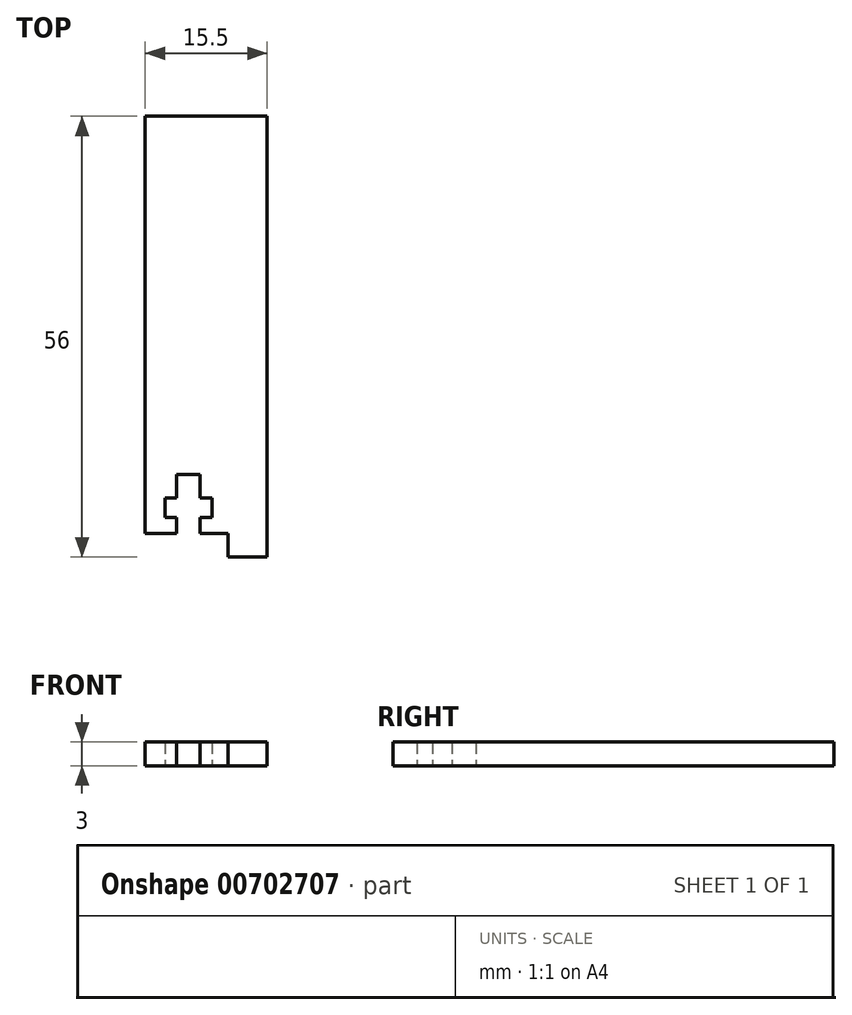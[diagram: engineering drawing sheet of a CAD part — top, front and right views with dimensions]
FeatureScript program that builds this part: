
annotation { "Feature Type Name" : "Feature", "Feature Type Description" : "" }
export const myFeature = defineFeature(function(context is Context, id is Id, definition is map)
    precondition{}
    {
        {
            var Q0;
            Q0=qCreatedBy(makeId("Top.planeOp"),FACE);
            var sketch = newSketch(context, id + "F0", { "sketchPlane" : qUnion([Q0])});
            skLineSegment(sketch, "E0", {"start": v(0, 0) * mm, "end": v(0, 53) * mm});
            skLineSegment(sketch, "E1", {"start": v(0, 53) * mm, "end": v(15.5, 53) * mm});
            skLineSegment(sketch, "E2", {"start": v(15.5, 53) * mm, "end": v(15.5, -3) * mm});
            skLineSegment(sketch, "E3", {"start": v(7, 0) * mm, "end": v(7, 2) * mm});
            skLineSegment(sketch, "E4", {"start": v(7, 2) * mm, "end": v(8.5, 2) * mm});
            skLineSegment(sketch, "E5", {"start": v(8.5, 2) * mm, "end": v(8.5, 4.5) * mm});
            skLineSegment(sketch, "E6", {"start": v(8.5, 4.5) * mm, "end": v(7, 4.5) * mm});
            skLineSegment(sketch, "E7", {"start": v(7, 4.5) * mm, "end": v(7, 7.5) * mm});
            skLineSegment(sketch, "E8", {"start": v(7, 7.5) * mm, "end": v(4, 7.5) * mm});
            skLineSegment(sketch, "E9", {"start": v(4, 7.5) * mm, "end": v(4, 4.5) * mm});
            skLineSegment(sketch, "E10", {"start": v(4, 4.5) * mm, "end": v(2.5, 4.5) * mm});
            skLineSegment(sketch, "E11", {"start": v(2.5, 4.5) * mm, "end": v(2.5, 2) * mm});
            skLineSegment(sketch, "E12", {"start": v(2.5, 2) * mm, "end": v(4, 2) * mm});
            skLineSegment(sketch, "E13", {"start": v(4, 2) * mm, "end": v(4, 0) * mm});
            skLineSegment(sketch, "E14", {"start": v(4, 0) * mm, "end": v(0, 0) * mm});
            skLineSegment(sketch, "E15", {"start": v(5.5, 7.5) * mm, "end": v(5.5, 0) * mm, "construction": true});
            skLineSegment(sketch, "E16", {"start": v(15.5, -3) * mm, "end": v(10.5, -3) * mm});
            skLineSegment(sketch, "E17", {"start": v(10.5, -3) * mm, "end": v(10.5, 0) * mm});
            skLineSegment(sketch, "E18", {"start": v(10.5, 0) * mm, "end": v(7, 0) * mm});
            skSolve(sketch);
        }
        {
            var Q0;
            Q0=makeQuery(id+"F0.imprint","IMPRINT",FACE,{"disambiguationData":[TD([[makeQuery(id+"F0.imprint","IMPRINT",EDGE,{"derivedFrom":sQuery(id+"F0.wireOp",EDGE,"E0")}),-1.0]])]});
            extrude(context, id + "F1", {"entities" : qUnion([Q0]), "depth" : 3 * mm, "offsetDistance" : 25.4 * mm});
        }
    });
